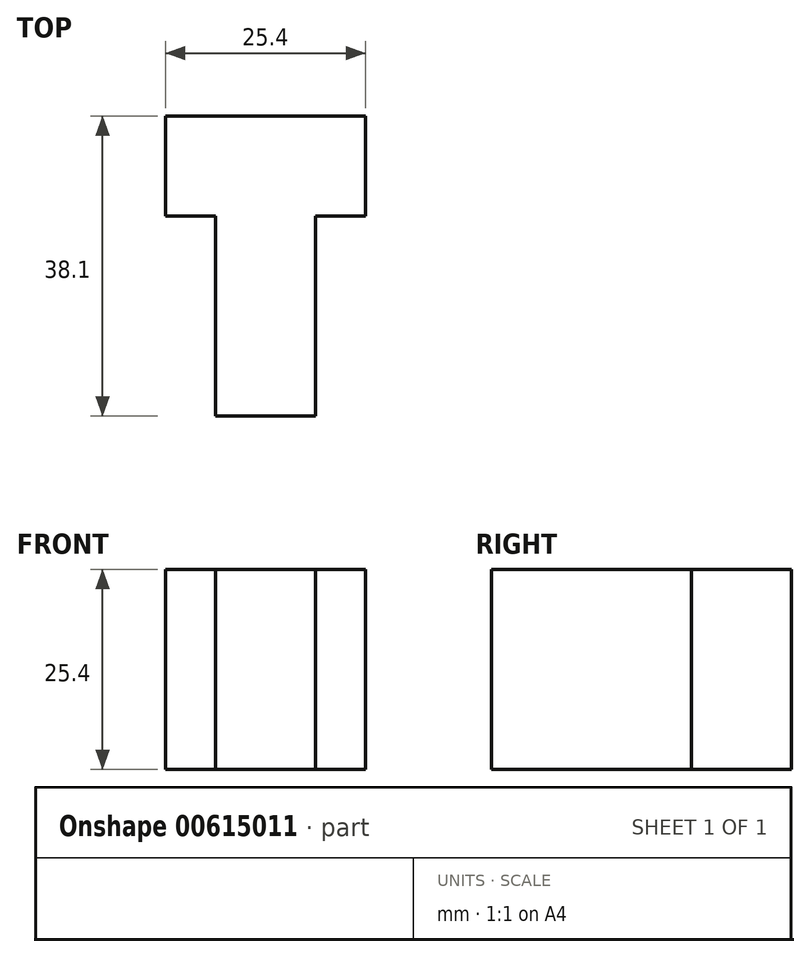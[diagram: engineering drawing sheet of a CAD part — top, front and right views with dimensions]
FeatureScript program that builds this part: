
annotation { "Feature Type Name" : "Feature", "Feature Type Description" : "" }
export const myFeature = defineFeature(function(context is Context, id is Id, definition is map)
    precondition{}
    {
        {
            var Q0;
            Q0=qCreatedBy(makeId("Top.planeOp"),FACE);
            var sketch = newSketch(context, id + "F0", { "sketchPlane" : qUnion([Q0])});
            skLineSegment(sketch, "E0", {"start": v(0, 0) * mm, "end": v(0, 25.4) * mm});
            skLineSegment(sketch, "E1", {"start": v(0, 25.4) * mm, "end": v(6.35, 25.4) * mm});
            skLineSegment(sketch, "E2", {"start": v(6.35, 25.4) * mm, "end": v(6.35, 38.1) * mm});
            skLineSegment(sketch, "E3", {"start": v(6.35, 38.1) * mm, "end": v(-19.05, 38.1) * mm});
            skLineSegment(sketch, "E4", {"start": v(-19.05, 38.1) * mm, "end": v(-19.05, 25.4) * mm});
            skLineSegment(sketch, "E5", {"start": v(-19.05, 25.4) * mm, "end": v(-12.7, 25.4) * mm});
            skLineSegment(sketch, "E6", {"start": v(-12.7, 25.4) * mm, "end": v(-12.7, 0) * mm});
            skLineSegment(sketch, "E7", {"start": v(-12.7, 0) * mm, "end": v(0, 0) * mm});
            skSolve(sketch);
        }
        {
            var Q0;
            Q0 = qSketchRegion(id + "F0", true);
            extrude(context, id + "F1", {"entities" : qUnion([Q0]), "oppositeDirection" : true, "depth" : 25.4 * mm, "offsetDistance" : 25.4 * mm});
        }
    });
